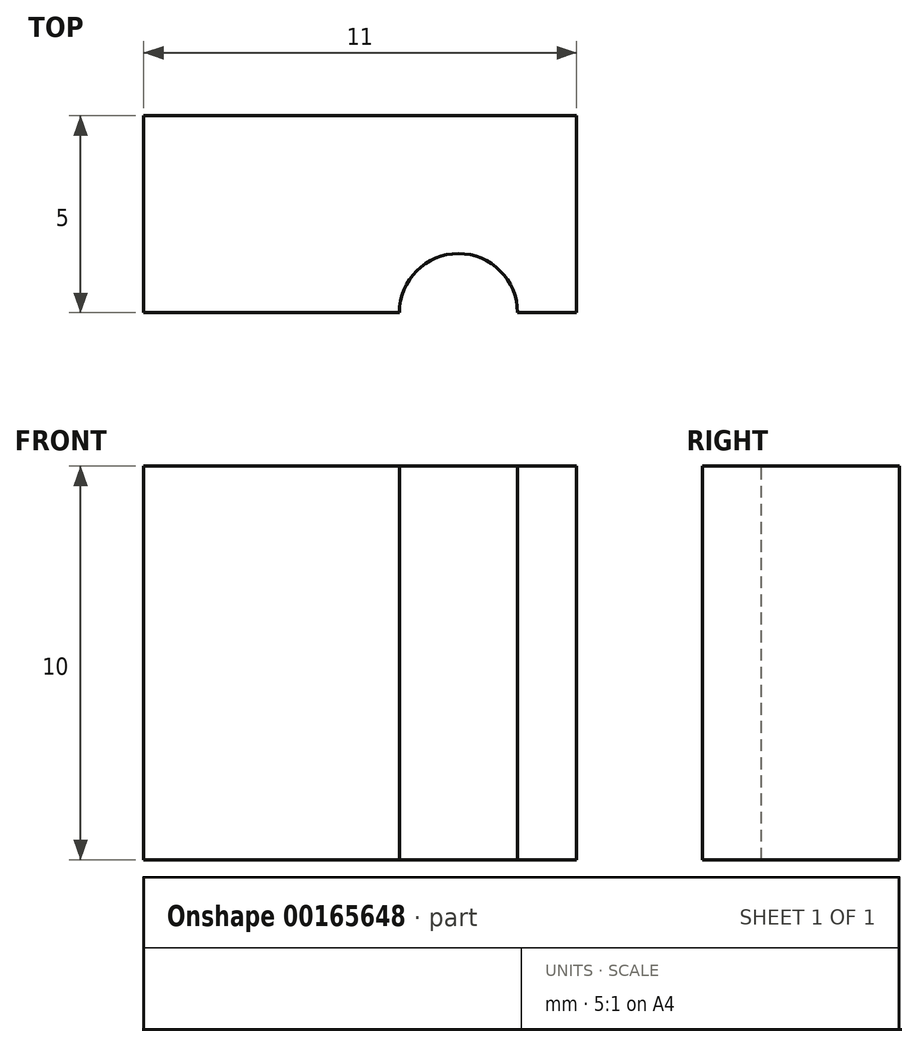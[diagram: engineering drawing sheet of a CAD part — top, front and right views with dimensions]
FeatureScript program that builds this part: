
annotation { "Feature Type Name" : "Feature", "Feature Type Description" : "" }
export const myFeature = defineFeature(function(context is Context, id is Id, definition is map)
    precondition{}
    {
        {
            var Q0;
            Q0=qCreatedBy(makeId("Top.planeOp"),FACE);
            var sketch = newSketch(context, id + "F0", { "sketchPlane" : qUnion([Q0])});
            skLineSegment(sketch, "E0.bottom", {"start": v(14.64, -2.5) * mm, "end": v(25.64, -2.5) * mm});
            skLineSegment(sketch, "E0.top", {"start": v(14.64, 2.5) * mm, "end": v(25.64, 2.5) * mm});
            skLineSegment(sketch, "E0.left", {"start": v(14.64, -2.5) * mm, "end": v(14.64, 2.5) * mm});
            skLineSegment(sketch, "E0.right", {"start": v(25.64, -2.5) * mm, "end": v(25.64, 2.5) * mm});
            skPoint(sketch, "E0.middle", {"position": v(20.14, 0) * mm});
            skSolve(sketch);
        }
        {
            var Q0;
            Q0=makeQuery(id+"F0.imprint","IMPRINT",FACE,{"disambiguationData":[TD([[makeQuery(id+"F0.imprint","IMPRINT",EDGE,{"derivedFrom":sQuery(id+"F0.wireOp",EDGE,"E0.bottom")}),1.0]])]});
            var Q1;
            Q1=makeQuery(id+"F0.imprint","IMPRINT",FACE,{"disambiguationData":[TD([[makeQuery(id+"F0.imprint","IMPRINT",EDGE,{"derivedFrom":sQuery(id+"F0.wireOp",EDGE,"E0.right")}),-1.0]])]});
            extrude(context, id + "F1", {"entities" : qUnion([Q0, Q1]), "depth" : 10 * mm, "offsetDistance" : 25 * mm});
        }
        {
            var Q0;
            Q0=makeQuery(id+"F1.opExtrude","CAP_FACE",FACE,{"disambiguationData":[OSD([sQuery(id+"F0.wireOp",EDGE,"E0.bottom"),sQuery(id+"F0.wireOp",EDGE,"E0.top"),sQuery(id+"F0.wireOp",EDGE,"E0.left"),sQuery(id+"F0.wireOp",EDGE,"E0.right")])],"isStart":false});
            var sketch = newSketch(context, id + "F2", { "sketchPlane" : qUnion([Q0]) });
            skCircle(sketch, "E1", {"center": v(22.64, -2.5) * mm, "radius": 1.5 * mm});
            skSolve(sketch);
        }
        {
            var Q0;
            {var subQ0=sQuery(id+"F2.wireOp",EDGE,"E1");var subQ1=makeQuery(id+"F1.opExtrude","CAP_EDGE",EDGE,{"disambiguationData":[OSD([sQuery(id+"F0.wireOp",EDGE,"E0.bottom")])],"isStart":false});var subQ2=makeQuery(id+"F2.imprint","INTERSECT",VERTEX,{"disambiguationData":[OD(0.0)],"derivedFrom":[subQ1,subQ0]});Q0=makeQuery(id+"F2.imprint","IMPRINT",FACE,{"disambiguationData":[TD([[makeQuery(id+"F2.imprint","IMPRINT",EDGE,{"disambiguationData":[TD([[subQ2,1.0]])],"derivedFrom":subQ0}),1.0]])]});}
            extrude(context, id + "F3", {"entities" : qUnion([Q0]), "operationType" : NewBodyOperationType.REMOVE, "endBound" : BoundingType.THROUGH_ALL, "oppositeDirection" : true, "depth" : 25 * mm, "offsetDistance" : 25 * mm});
        }
    });
